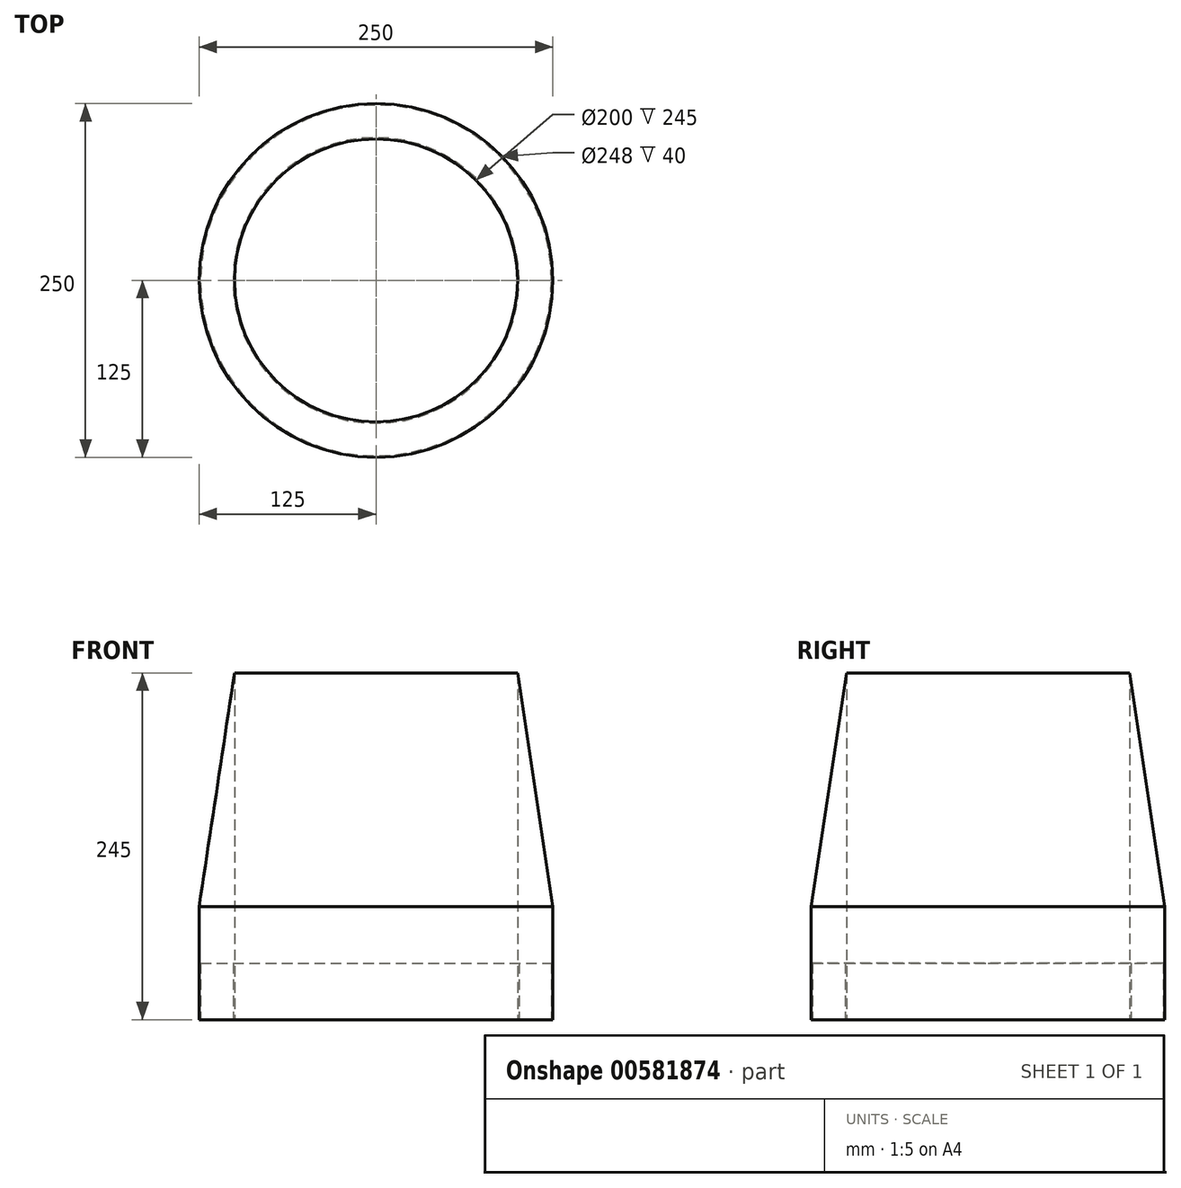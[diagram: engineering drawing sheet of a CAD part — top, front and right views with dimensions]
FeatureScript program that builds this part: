
annotation { "Feature Type Name" : "Feature", "Feature Type Description" : "" }
export const myFeature = defineFeature(function(context is Context, id is Id, definition is map)
    precondition{}
    {
        {
            var Q0;
            Q0=qCreatedBy(makeId("Front.planeOp"),FACE);
            var sketch = newSketch(context, id + "F0", { "sketchPlane" : qUnion([Q0])});
            skLineSegment(sketch, "E0", {"start": v(0, -139.25) * mm, "end": v(0, 240.83) * mm, "construction": true});
            skLineSegment(sketch, "E1", {"start": v(-100, -67.22) * mm, "end": v(-100, 177.78) * mm});
            skLineSegment(sketch, "E2", {"start": v(-100, 177.78) * mm, "end": v(-125, 12.78) * mm});
            skLineSegment(sketch, "E3", {"start": v(-125, 12.78) * mm, "end": v(-125, -67.22) * mm});
            skLineSegment(sketch, "E4", {"start": v(-125, -67.22) * mm, "end": v(-124, -67.22) * mm});
            skLineSegment(sketch, "E5", {"start": v(-124, -67.22) * mm, "end": v(-124, -27.22) * mm});
            skLineSegment(sketch, "E6", {"start": v(-124, -27.22) * mm, "end": v(-101, -27.22) * mm});
            skLineSegment(sketch, "E7", {"start": v(-101, -27.22) * mm, "end": v(-101, -67.22) * mm});
            skLineSegment(sketch, "E8", {"start": v(-101, -67.22) * mm, "end": v(-100, -67.22) * mm});
            skSolve(sketch);
        }
        {
            var Q0;
            Q0=qSketchRegion(id+"F0",true);
            var Q1;
            Q1=sQuery(id+"F0.wireOp",EDGE,"E0");
            revolve(context, id + "F1", {"entities" : qUnion([Q0]), "axis" : qUnion([Q1]), "revolveType" : RevolveType.FULL});
        }
    });
